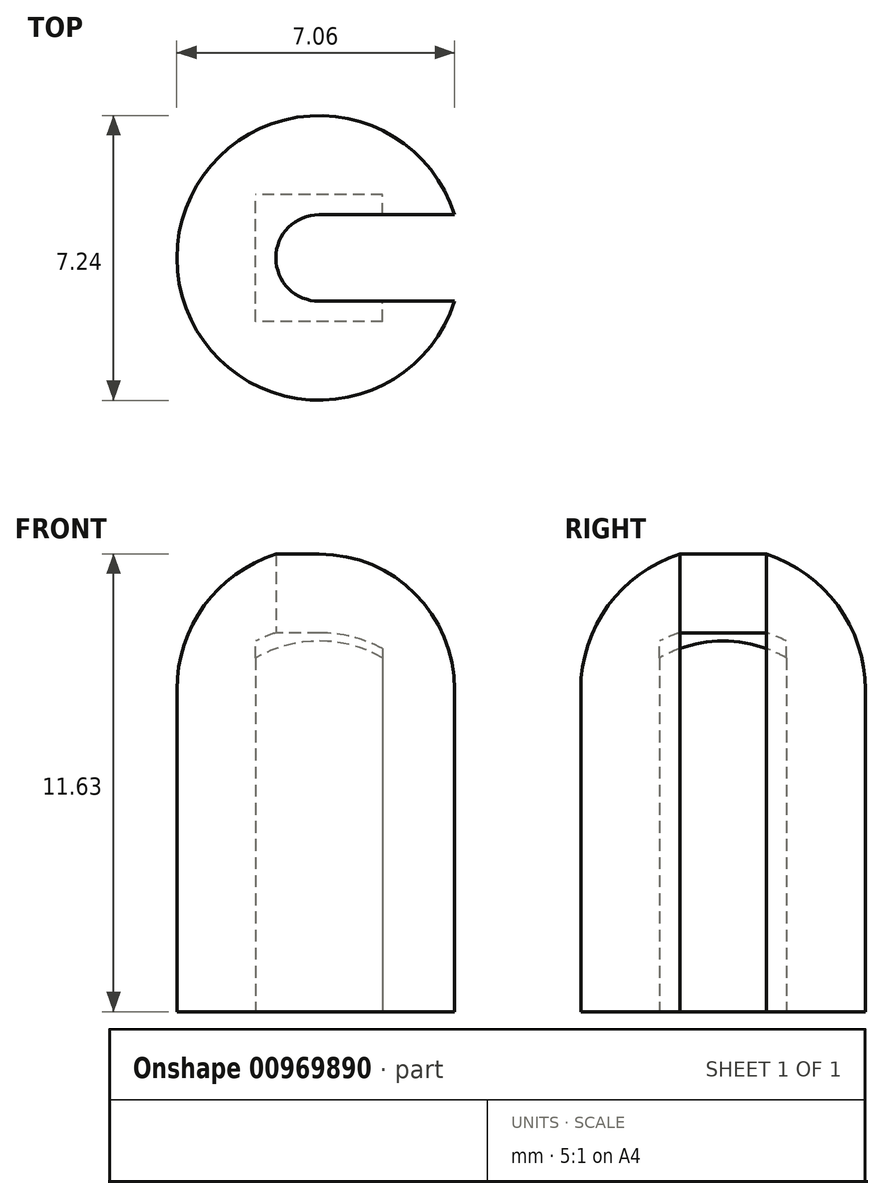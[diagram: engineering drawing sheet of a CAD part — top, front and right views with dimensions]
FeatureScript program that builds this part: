
annotation { "Feature Type Name" : "Feature", "Feature Type Description" : "" }
export const myFeature = defineFeature(function(context is Context, id is Id, definition is map)
    precondition{}
    {
        {
            var Q0;
            Q0=qCreatedBy(makeId("Front.planeOp"),FACE);
            var sketch = newSketch(context, id + "F0", { "sketchPlane" : qUnion([Q0])});
            skLineSegment(sketch, "E0", {"start": v(0, 0) * mm, "end": v(3.61, 0) * mm});
            skLineSegment(sketch, "E1", {"start": v(3.62, 0) * mm, "end": v(3.62, 8.18) * mm});
            skArc(sketch, "E2", {"start": v(3.62, 8.18) * mm, "mid": v(2.56, 10.74) * mm, "end": v(0, 11.8) * mm});
            skLineSegment(sketch, "E3", {"start": v(0, -3.92) * mm, "end": v(0, 15.43) * mm, "construction": true});
            skLineSegment(sketch, "E4", {"start": v(0, 11.8) * mm, "end": v(0, 0) * mm});
            skSolve(sketch);
        }
        {
            var Q0;
            Q0 = qSketchRegion(id + "F0", true);
            var Q1;
            Q1=sQuery(id+"F0.wireOp",EDGE,"E3");
            revolve(context, id + "F1", {"surfaceOperationType" : NewSurfaceOperationType.NEW, "entities" : qUnion([Q0]), "axis" : qUnion([Q1]), "revolveType" : RevolveType.FULL});
        }
        {
            var Q0;
            Q0=makeQuery(id+"F1.opRevolve","SWEPT_FACE",FACE,{"disambiguationData":[OSD([sQuery(id+"F0.wireOp",EDGE,"E0")])]});
            var sketch = newSketch(context, id + "F2", { "sketchPlane" : qUnion([Q0])});
            skLineSegment(sketch, "E5.bottom", {"start": v(1.62, 1.62) * mm, "end": v(-1.62, 1.62) * mm});
            skLineSegment(sketch, "E5.top", {"start": v(1.62, -1.61) * mm, "end": v(-1.61, -1.62) * mm});
            skLineSegment(sketch, "E5.left", {"start": v(1.62, 1.62) * mm, "end": v(1.62, -1.61) * mm});
            skLineSegment(sketch, "E5.right", {"start": v(-1.62, 1.62) * mm, "end": v(-1.61, -1.62) * mm});
            skLineSegment(sketch, "E6", {"start": v(1.62, 1.62) * mm, "end": v(-1.62, -1.62) * mm, "construction": true});
            skSolve(sketch);
        }
        {
            var Q0;
            Q0=makeQuery(id+"F2.imprint","IMPRINT",FACE,{"disambiguationData":[TD([[makeQuery(id+"F2.imprint","IMPRINT",EDGE,{"derivedFrom":sQuery(id+"F2.wireOp",EDGE,"E5.bottom")}),1.0]])]});
            extrude(context, id + "F3", {"entities" : qUnion([Q0]), "operationType" : NewBodyOperationType.REMOVE, "endBound" : BoundingType.UP_TO_NEXT, "oppositeDirection" : true, "depth" : 8 * mm, "hasOffset" : true, "offsetDistance" : 2 * mm});
        }
        {
            var Q0;
            Q0=makeQuery(id+"F1.opRevolve","SWEPT_FACE",FACE,{"disambiguationData":[OSD([sQuery(id+"F0.wireOp",EDGE,"E0")])]});
            var sketch = newSketch(context, id + "F4", { "sketchPlane" : qUnion([Q0])});
            skLineSegment(sketch, "E7.bottom", {"start": v(0, 1.1) * mm, "end": v(3.62, 1.1) * mm});
            skLineSegment(sketch, "E7.top", {"start": v(0, -1.1) * mm, "end": v(3.62, -1.1) * mm});
            skLineSegment(sketch, "E7.right", {"start": v(3.62, 1.1) * mm, "end": v(3.62, -1.1) * mm});
            skArc(sketch, "E8", {"start": v(0, 1.1) * mm, "mid": v(-1.1, 0) * mm, "end": v(0, -1.1) * mm});
            skSolve(sketch);
        }
        {
            var Q0;
            Q0 = qSketchRegion(id + "F4", true);
            extrude(context, id + "F5", {"entities" : qUnion([Q0]), "operationType" : NewBodyOperationType.REMOVE, "endBound" : BoundingType.THROUGH_ALL, "oppositeDirection" : true, "depth" : 25 * mm, "offsetDistance" : 25 * mm});
        }
    });
